# Revit family: Thorn EQUALINE MINI
name_source: partatom
category: Lighting Fixtures
revit_build: Autodesk Revit 2016 (Build: 20150220_1215(x64)
units: mm (PartAtom-declared; Revit-internal decimal feet)

## family parameters
Cut with Voids When Loaded = No
Host = Face
Light Source = Yes
OmniClass Number = 23.80.70.11
OmniClass Title = Luminaries for Internal Lighting
Part Type = Normal
Room Calculation Point = No
Round Connector Dimension = Use Diameter
Shared = No

## types (2) — shared parameters
Assembly Code = D5020200
Body = Thorn_Metal_White
Color Filter = 16777215
Cover = Thorn_PMMA
Description = LED luminaire
Dimming Lamp Color Temperature Shift = <None>
Emit Shape Visible in Rendering = No
Emit from Rectangle Length = 37 mm  [stored 0.121391 ft]
Height = 60 mm  [stored 0.19685 ft]
Lamp = LED
Manufacturer = Thorn Lighting
Tilt Angle = -90.00°
Voltage = 230 V
Width = 37 mm  [stored 0.121391 ft]
zero-valued in all types: Default Elevation

## per-type parameters (varying)
| type | Apparent Load | Emit from Rectangle Width | Length | Model | Photometric Web File | URL |
| EQUAMINI L580 | 10 VA | 580 mm  [stored 1.90289 ft] | 580 mm  [stored 1.90289 ft] | 96630771 | 96630771_(STD).IES | www.thornlighting.com/96630771 |
| EQUAMINI L1180 | 18 VA | 1180 mm  [stored 3.87139 ft] | 1180 mm  [stored 3.87139 ft] | 96630769 | 96630769_(STD).IES | www.thornlighting.com/96630769 |

note: [stored X ft] marks values corroborated as IEEE doubles in the binary element streams (Revit-internal decimal feet)

## geometry (parser evidence)
native form markers: Sweep x4
no freeform markers — native parametric forms only
